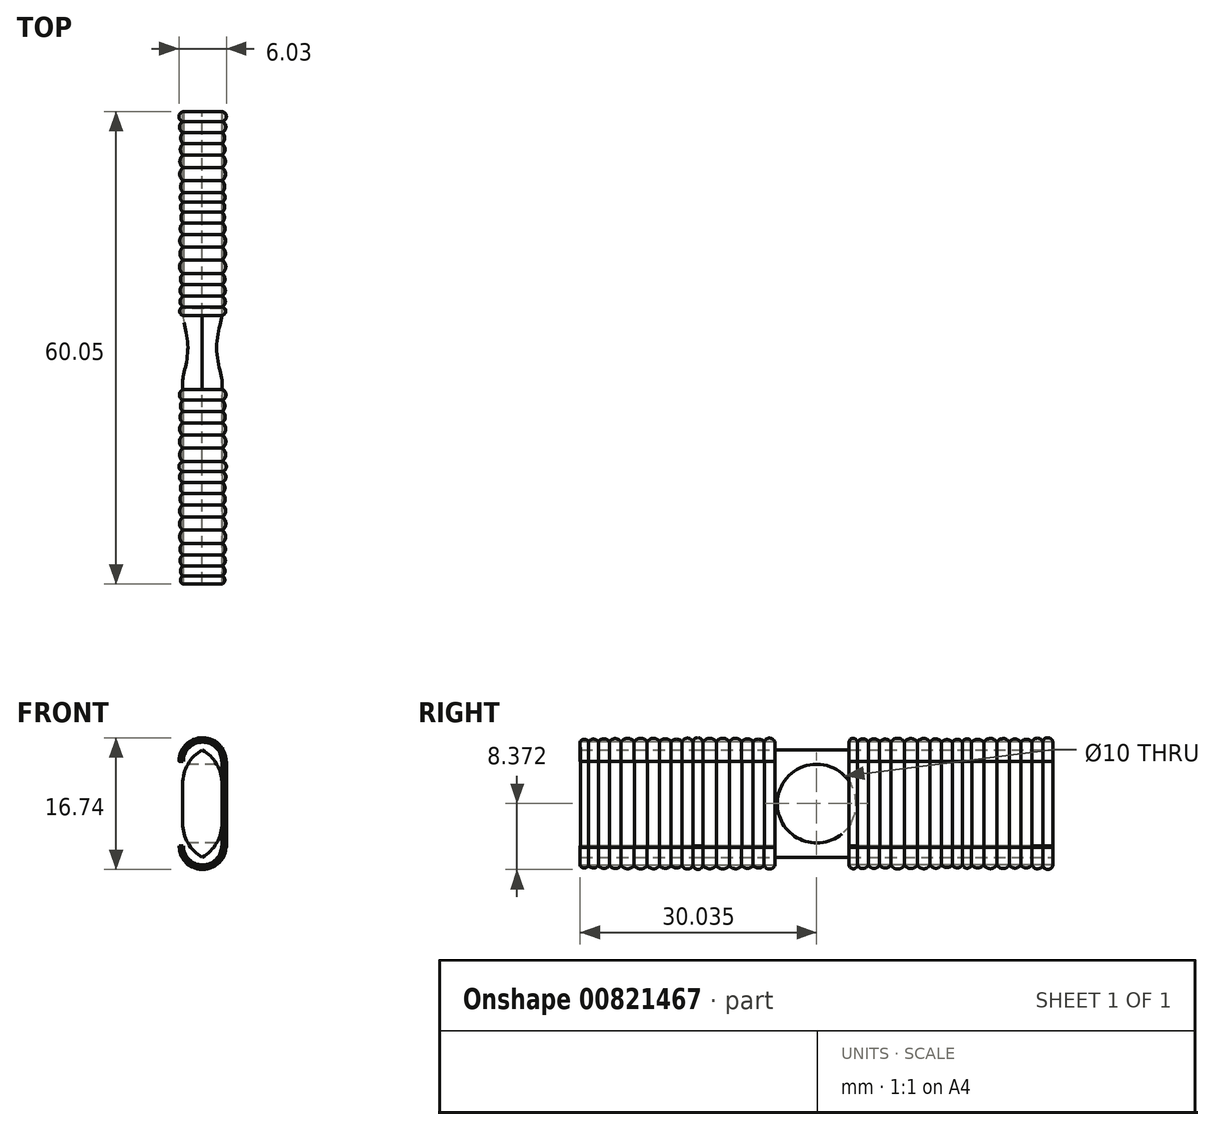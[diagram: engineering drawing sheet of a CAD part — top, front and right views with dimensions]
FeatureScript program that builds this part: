
annotation { "Feature Type Name" : "Feature", "Feature Type Description" : "" }
export const myFeature = defineFeature(function(context is Context, id is Id, definition is map)
    precondition{}
    {
        {
            var Q0;
            Q0=qCreatedBy(makeId("Right.planeOp"),FACE);
            var sketch = newSketch(context, id + "F0", { "sketchPlane" : qUnion([Q0])});
            skLineSegment(sketch, "E0.bottom", {"start": v(-22.09, 0.4) * mm, "end": v(37.91, 0.4) * mm});
            skLineSegment(sketch, "E0.top", {"start": v(-22.09, -14.6) * mm, "end": v(37.91, -14.6) * mm});
            skLineSegment(sketch, "E0.left", {"start": v(-22.09, 0.4) * mm, "end": v(-22.09, -14.6) * mm});
            skLineSegment(sketch, "E0.right", {"start": v(37.91, 0.4) * mm, "end": v(37.91, -14.6) * mm});
            skCircle(sketch, "E1", {"center": v(7.91, -7.1) * mm, "radius": 5 * mm});
            skPoint(sketch, "E1.centerSnap0", {"position": v(37.91, -7.1) * mm});
            skPoint(sketch, "E1.centerSnap1", {"position": v(7.91, 0.4) * mm});
            skLineSegment(sketch, "E2", {"start": v(37.91, -7.1) * mm, "end": v(7.91, -7.1) * mm});
            skSolve(sketch);
        }
        {
            var Q0;
            Q0=makeQuery(id+"F0.imprint","IMPRINT",FACE,{"disambiguationData":[TD([[makeQuery(id+"F0.imprint","IMPRINT",EDGE,{"derivedFrom":sQuery(id+"F0.wireOp",EDGE,"E0.bottom")}),-1.0]])]});
            extrude(context, id + "F1", {"entities" : qUnion([Q0]), "depth" : 5 * mm, "offsetDistance" : 25.4 * mm});
        }
        {
            var Q0;
            Q0=makeQuery(id+"F1.opExtrude","CAP_EDGE",EDGE,{"disambiguationData":[OSD([sQuery(id+"F0.wireOp",EDGE,"E0.top")])],"isStart":true});
            var Q1;
            Q1=makeQuery(id+"F1.opExtrude","CAP_EDGE",EDGE,{"disambiguationData":[OSD([sQuery(id+"F0.wireOp",EDGE,"E0.top")])],"isStart":false});
            var Q2;
            Q2=makeQuery(id+"F1.opExtrude","CAP_EDGE",EDGE,{"disambiguationData":[OSD([sQuery(id+"F0.wireOp",EDGE,"E0.bottom")])],"isStart":false});
            var Q3;
            Q3=makeQuery(id+"F1.opExtrude","CAP_EDGE",EDGE,{"disambiguationData":[OSD([sQuery(id+"F0.wireOp",EDGE,"E0.bottom")])],"isStart":true});
            fillet(context, id + "F2", {"entities" : qUnion([Q0, Q1, Q2, Q3]), "radius" : 5 * mm, "tangentPropagation" : true, "allowEdgeOverflow" : false});
        }
        {
            var Q0;
            Q0=qCreatedBy(makeId("Top.planeOp"),FACE);
            var sketch = newSketch(context, id + "F3", { "sketchPlane" : qUnion([Q0])});
            skLineSegment(sketch, "E3", {"start": v(5, 37.93) * mm, "end": v(5, 12.02) * mm});
            skLineSegment(sketch, "E4", {"start": v(5.04, 3.85) * mm, "end": v(5.04, -22.1) * mm});
            skArc(sketch, "E5", {"start": v(5, 36.67) * mm, "mid": v(5.57, 37.3) * mm, "end": v(5, 37.93) * mm});
            skArc(sketch, "E6", {"start": v(5, 35.28) * mm, "mid": v(5.5, 35.97) * mm, "end": v(5, 36.67) * mm});
            skArc(sketch, "E7", {"start": v(5, 33.85) * mm, "mid": v(5.36, 34.56) * mm, "end": v(5, 35.28) * mm});
            skArc(sketch, "E8", {"start": v(5, 32.4) * mm, "mid": v(5.4, 33.12) * mm, "end": v(5, 33.85) * mm});
            skArc(sketch, "E9", {"start": v(5, 30.82) * mm, "mid": v(5.45, 31.6) * mm, "end": v(5, 32.4) * mm});
            skArc(sketch, "E10", {"start": v(5, 29.16) * mm, "mid": v(5.47, 29.99) * mm, "end": v(5, 30.82) * mm});
            skArc(sketch, "E11", {"start": v(5, 27.62) * mm, "mid": v(5.36, 28.4) * mm, "end": v(5, 29.16) * mm});
            skArc(sketch, "E12", {"start": v(5, 26.42) * mm, "mid": v(5.42, 27.02) * mm, "end": v(5, 27.62) * mm});
            skArc(sketch, "E13", {"start": v(5, 25.16) * mm, "mid": v(5.37, 25.8) * mm, "end": v(5, 26.42) * mm});
            skArc(sketch, "E14", {"start": v(5, 23.78) * mm, "mid": v(5.32, 24.47) * mm, "end": v(5, 25.16) * mm});
            skArc(sketch, "E15", {"start": v(5, 22.32) * mm, "mid": v(5.41, 23.05) * mm, "end": v(5, 23.78) * mm});
            skArc(sketch, "E16", {"start": v(5, 20.72) * mm, "mid": v(5.47, 21.52) * mm, "end": v(5, 22.32) * mm});
            skArc(sketch, "E17", {"start": v(5, 19.09) * mm, "mid": v(5.45, 19.9) * mm, "end": v(5, 20.72) * mm});
            skArc(sketch, "E18", {"start": v(5, 17.35) * mm, "mid": v(5.5, 18.22) * mm, "end": v(5, 19.09) * mm});
            skArc(sketch, "E19", {"start": v(5, 15.93) * mm, "mid": v(5.39, 16.64) * mm, "end": v(5, 17.35) * mm});
            skArc(sketch, "E20", {"start": v(5, 14.48) * mm, "mid": v(5.43, 15.2) * mm, "end": v(5, 15.93) * mm});
            skArc(sketch, "E21", {"start": v(5, 13.12) * mm, "mid": v(5.44, 13.8) * mm, "end": v(5, 14.48) * mm});
            skArc(sketch, "E22", {"start": v(5, 12.02) * mm, "mid": v(5.48, 12.57) * mm, "end": v(5, 13.12) * mm});
            skLineSegment(sketch, "E23", {"start": v(5, 12.02) * mm, "end": v(5.04, 3.85) * mm});
            skLineSegment(sketch, "E24", {"start": v(5.02, 7.94) * mm, "end": v(0, 7.91) * mm});
            skArc(sketch, "E25", {"start": v(5.04, 2.63) * mm, "mid": v(5.57, 3.25) * mm, "end": v(5.04, 3.88) * mm});
            skArc(sketch, "E26", {"start": v(5.04, 1.26) * mm, "mid": v(5.51, 1.94) * mm, "end": v(5.04, 2.63) * mm});
            skArc(sketch, "E27", {"start": v(5.04, -0.16) * mm, "mid": v(5.38, 0.55) * mm, "end": v(5.04, 1.26) * mm});
            skArc(sketch, "E28", {"start": v(5.04, -1.6) * mm, "mid": v(5.43, -0.88) * mm, "end": v(5.04, -0.16) * mm});
            skArc(sketch, "E29", {"start": v(5.04, -3.17) * mm, "mid": v(5.49, -2.39) * mm, "end": v(5.04, -1.6) * mm});
            skArc(sketch, "E30", {"start": v(5.04, -4.82) * mm, "mid": v(5.5, -4) * mm, "end": v(5.04, -3.17) * mm});
            skArc(sketch, "E31", {"start": v(5.04, -6.5) * mm, "mid": v(5.48, -5.66) * mm, "end": v(5.04, -4.82) * mm});
            skArc(sketch, "E32", {"start": v(5.04, -7.8) * mm, "mid": v(5.57, -7.17) * mm, "end": v(5.04, -6.55) * mm});
            skArc(sketch, "E33", {"start": v(5.04, -9.16) * mm, "mid": v(5.51, -8.48) * mm, "end": v(5.04, -7.8) * mm});
            skArc(sketch, "E34", {"start": v(5.04, -10.58) * mm, "mid": v(5.38, -9.87) * mm, "end": v(5.04, -9.16) * mm});
            skArc(sketch, "E35", {"start": v(5.04, -12.03) * mm, "mid": v(5.43, -11.3) * mm, "end": v(5.04, -10.58) * mm});
            skArc(sketch, "E36", {"start": v(5.04, -13.6) * mm, "mid": v(5.49, -12.81) * mm, "end": v(5.04, -12.03) * mm});
            skArc(sketch, "E37", {"start": v(5.04, -15.25) * mm, "mid": v(5.5, -14.42) * mm, "end": v(5.04, -13.6) * mm});
            skArc(sketch, "E38", {"start": v(5.04, -16.92) * mm, "mid": v(5.48, -16.08) * mm, "end": v(5.04, -15.25) * mm});
            skArc(sketch, "E39", {"start": v(5.04, -18.4) * mm, "mid": v(5.45, -17.66) * mm, "end": v(5.04, -16.92) * mm});
            skArc(sketch, "E40", {"start": v(5.04, -19.8) * mm, "mid": v(5.43, -19.1) * mm, "end": v(5.04, -18.4) * mm});
            skArc(sketch, "E41", {"start": v(5.04, -21.06) * mm, "mid": v(5.39, -20.43) * mm, "end": v(5.04, -19.8) * mm});
            skArc(sketch, "E42", {"start": v(5.04, -22.1) * mm, "mid": v(5.37, -21.58) * mm, "end": v(5.04, -21.06) * mm});
            skArc(sketch, "E43.MirrorCS", {"start": v(0, 14.48) * mm, "mid": v(-0.43, 15.2) * mm, "end": v(0, 15.93) * mm});
            skArc(sketch, "E44.MirrorCS", {"start": v(-0.04, -0.16) * mm, "mid": v(-0.38, 0.55) * mm, "end": v(-0.04, 1.26) * mm});
            skArc(sketch, "E45.MirrorCS", {"start": v(0, 23.78) * mm, "mid": v(-0.32, 24.47) * mm, "end": v(0, 25.16) * mm});
            skArc(sketch, "E46.MirrorCS", {"start": v(0, 26.42) * mm, "mid": v(-0.42, 27.02) * mm, "end": v(0, 27.62) * mm});
            skArc(sketch, "E47.MirrorCS", {"start": v(0, 33.85) * mm, "mid": v(-0.36, 34.56) * mm, "end": v(0, 35.28) * mm});
            skArc(sketch, "E48.MirrorCS", {"start": v(0, 25.16) * mm, "mid": v(-0.37, 25.8) * mm, "end": v(0, 26.42) * mm});
            skArc(sketch, "E49.MirrorCS", {"start": v(-0.04, -12.03) * mm, "mid": v(-0.43, -11.3) * mm, "end": v(-0.04, -10.58) * mm});
            skLineSegment(sketch, "E50.MirrorCS", {"start": v(0, 37.93) * mm, "end": v(0, 12.02) * mm});
            skArc(sketch, "E51.MirrorCS", {"start": v(-0.04, -6.5) * mm, "mid": v(-0.48, -5.66) * mm, "end": v(-0.04, -4.82) * mm});
            skArc(sketch, "E52.MirrorCS", {"start": v(0, 22.32) * mm, "mid": v(-0.41, 23.05) * mm, "end": v(0, 23.78) * mm});
            skArc(sketch, "E53.MirrorCS", {"start": v(-0.04, -16.92) * mm, "mid": v(-0.48, -16.08) * mm, "end": v(-0.04, -15.25) * mm});
            skArc(sketch, "E54.MirrorCS", {"start": v(-0.04, -3.17) * mm, "mid": v(-0.49, -2.39) * mm, "end": v(-0.04, -1.6) * mm});
            skArc(sketch, "E55.MirrorCS", {"start": v(0, 35.28) * mm, "mid": v(-0.5, 35.97) * mm, "end": v(0, 36.67) * mm});
            skArc(sketch, "E56.MirrorCS", {"start": v(0, 13.12) * mm, "mid": v(-0.44, 13.8) * mm, "end": v(0, 14.48) * mm});
            skArc(sketch, "E57.MirrorCS", {"start": v(0, 27.62) * mm, "mid": v(-0.36, 28.4) * mm, "end": v(0, 29.16) * mm});
            skArc(sketch, "E58.MirrorCS", {"start": v(0, 32.4) * mm, "mid": v(-0.4, 33.12) * mm, "end": v(0, 33.85) * mm});
            skArc(sketch, "E59.MirrorCS", {"start": v(0, 12.02) * mm, "mid": v(-0.48, 12.57) * mm, "end": v(0, 13.12) * mm});
            skArc(sketch, "E60.MirrorCS", {"start": v(0, 15.93) * mm, "mid": v(-0.39, 16.64) * mm, "end": v(0, 17.35) * mm});
            skArc(sketch, "E61.MirrorCS", {"start": v(0, 17.35) * mm, "mid": v(-0.5, 18.22) * mm, "end": v(0, 19.09) * mm});
            skArc(sketch, "E62.MirrorCS", {"start": v(-0.04, 2.63) * mm, "mid": v(-0.57, 3.25) * mm, "end": v(-0.04, 3.88) * mm});
            skArc(sketch, "E63.MirrorCS", {"start": v(-0.04, 1.26) * mm, "mid": v(-0.51, 1.94) * mm, "end": v(-0.04, 2.63) * mm});
            skArc(sketch, "E64.MirrorCS", {"start": v(0, 36.67) * mm, "mid": v(-0.57, 37.3) * mm, "end": v(0, 37.93) * mm});
            skArc(sketch, "E65.MirrorCS", {"start": v(0, 19.09) * mm, "mid": v(-0.45, 19.9) * mm, "end": v(0, 20.72) * mm});
            skArc(sketch, "E66.MirrorCS", {"start": v(-0.04, -10.58) * mm, "mid": v(-0.38, -9.87) * mm, "end": v(-0.04, -9.16) * mm});
            skArc(sketch, "E67.MirrorCS", {"start": v(-0.04, -4.82) * mm, "mid": v(-0.5, -4) * mm, "end": v(-0.04, -3.17) * mm});
            skArc(sketch, "E68.MirrorCS", {"start": v(-0.04, -1.6) * mm, "mid": v(-0.43, -0.88) * mm, "end": v(-0.04, -0.16) * mm});
            skArc(sketch, "E69.MirrorCS", {"start": v(0, 30.82) * mm, "mid": v(-0.45, 31.6) * mm, "end": v(0, 32.4) * mm});
            skArc(sketch, "E70.MirrorCS", {"start": v(-0.04, -15.25) * mm, "mid": v(-0.5, -14.42) * mm, "end": v(-0.04, -13.6) * mm});
            skArc(sketch, "E71.MirrorCS", {"start": v(0, 20.72) * mm, "mid": v(-0.47, 21.52) * mm, "end": v(0, 22.32) * mm});
            skArc(sketch, "E72.MirrorCS", {"start": v(-0.04, -19.8) * mm, "mid": v(-0.43, -19.1) * mm, "end": v(-0.04, -18.4) * mm});
            skArc(sketch, "E73.MirrorCS", {"start": v(-0.04, -9.16) * mm, "mid": v(-0.51, -8.48) * mm, "end": v(-0.04, -7.8) * mm});
            skArc(sketch, "E74.MirrorCS", {"start": v(0, 29.16) * mm, "mid": v(-0.47, 29.99) * mm, "end": v(0, 30.82) * mm});
            skArc(sketch, "E75.MirrorCS", {"start": v(-0.04, -13.6) * mm, "mid": v(-0.49, -12.81) * mm, "end": v(-0.04, -12.03) * mm});
            skArc(sketch, "E76.MirrorCS", {"start": v(-0.04, -7.8) * mm, "mid": v(-0.57, -7.17) * mm, "end": v(-0.04, -6.55) * mm});
            skArc(sketch, "E77.MirrorCS", {"start": v(-0.04, -18.4) * mm, "mid": v(-0.45, -17.66) * mm, "end": v(-0.04, -16.92) * mm});
            skLineSegment(sketch, "E78.MirrorCS", {"start": v(0, 12.02) * mm, "end": v(-0.04, 3.85) * mm});
            skArc(sketch, "E79.MirrorCS", {"start": v(-0.04, -21.06) * mm, "mid": v(-0.39, -20.43) * mm, "end": v(-0.04, -19.8) * mm});
            skArc(sketch, "E80.MirrorCS", {"start": v(-0.04, -22.1) * mm, "mid": v(-0.37, -21.58) * mm, "end": v(-0.04, -21.06) * mm});
            skLineSegment(sketch, "E81", {"start": v(-0.04, 3.88) * mm, "end": v(-0.04, -22.1) * mm});
            skSolve(sketch);
        }
        {
            var Q0;
            {var subQ0=sQuery(id+"F3.wireOp",EDGE,"E10");Q0=makeQuery(id+"F3.imprint","IMPRINT",FACE,{"disambiguationData":[TD([[makeQuery(id+"F3.imprint","IMPRINT",EDGE,{"derivedFrom":subQ0}),1.0]])]});}
            var Q1;
            {var subQ0=sQuery(id+"F3.wireOp",EDGE,"E66.MirrorCS");Q1=makeQuery(id+"F3.imprint","IMPRINT",FACE,{"disambiguationData":[TD([[makeQuery(id+"F3.imprint","IMPRINT",EDGE,{"derivedFrom":subQ0}),-1.0]])]});}
            var Q2;
            {var subQ0=sQuery(id+"F3.wireOp",EDGE,"E71.MirrorCS");Q2=makeQuery(id+"F3.imprint","IMPRINT",FACE,{"disambiguationData":[TD([[makeQuery(id+"F3.imprint","IMPRINT",EDGE,{"derivedFrom":subQ0}),-1.0]])]});}
            var Q3;
            {var subQ0=sQuery(id+"F3.wireOp",EDGE,"E31");Q3=makeQuery(id+"F3.imprint","IMPRINT",FACE,{"disambiguationData":[TD([[makeQuery(id+"F3.imprint","IMPRINT",EDGE,{"derivedFrom":subQ0}),1.0]])]});}
            var Q4;
            {var subQ0=sQuery(id+"F3.wireOp",EDGE,"E35");Q4=makeQuery(id+"F3.imprint","IMPRINT",FACE,{"disambiguationData":[TD([[makeQuery(id+"F3.imprint","IMPRINT",EDGE,{"derivedFrom":subQ0}),1.0]])]});}
            var Q5;
            {var subQ0=sQuery(id+"F3.wireOp",EDGE,"E70.MirrorCS");Q5=makeQuery(id+"F3.imprint","IMPRINT",FACE,{"disambiguationData":[TD([[makeQuery(id+"F3.imprint","IMPRINT",EDGE,{"derivedFrom":subQ0}),-1.0]])]});}
            var Q6;
            {var subQ0=sQuery(id+"F3.wireOp",EDGE,"E19");Q6=makeQuery(id+"F3.imprint","IMPRINT",FACE,{"disambiguationData":[TD([[makeQuery(id+"F3.imprint","IMPRINT",EDGE,{"derivedFrom":subQ0}),1.0]])]});}
            var Q7;
            {var subQ0=sQuery(id+"F3.wireOp",EDGE,"E15");Q7=makeQuery(id+"F3.imprint","IMPRINT",FACE,{"disambiguationData":[TD([[makeQuery(id+"F3.imprint","IMPRINT",EDGE,{"derivedFrom":subQ0}),1.0]])]});}
            var Q8;
            {var subQ0=sQuery(id+"F3.wireOp",EDGE,"E14");Q8=makeQuery(id+"F3.imprint","IMPRINT",FACE,{"disambiguationData":[TD([[makeQuery(id+"F3.imprint","IMPRINT",EDGE,{"derivedFrom":subQ0}),1.0]])]});}
            var Q9;
            {var subQ0=sQuery(id+"F3.wireOp",EDGE,"E18");Q9=makeQuery(id+"F3.imprint","IMPRINT",FACE,{"disambiguationData":[TD([[makeQuery(id+"F3.imprint","IMPRINT",EDGE,{"derivedFrom":subQ0}),1.0]])]});}
            var Q10;
            {var subQ0=sQuery(id+"F3.wireOp",EDGE,"E53.MirrorCS");Q10=makeQuery(id+"F3.imprint","IMPRINT",FACE,{"disambiguationData":[TD([[makeQuery(id+"F3.imprint","IMPRINT",EDGE,{"derivedFrom":subQ0}),-1.0]])]});}
            var Q11;
            {var subQ0=sQuery(id+"F3.wireOp",EDGE,"E54.MirrorCS");Q11=makeQuery(id+"F3.imprint","IMPRINT",FACE,{"disambiguationData":[TD([[makeQuery(id+"F3.imprint","IMPRINT",EDGE,{"derivedFrom":subQ0}),-1.0]])]});}
            var Q12;
            {var subQ0=sQuery(id+"F3.wireOp",EDGE,"E65.MirrorCS");Q12=makeQuery(id+"F3.imprint","IMPRINT",FACE,{"disambiguationData":[TD([[makeQuery(id+"F3.imprint","IMPRINT",EDGE,{"derivedFrom":subQ0}),-1.0]])]});}
            var Q13;
            {var subQ0=sQuery(id+"F3.wireOp",EDGE,"E67.MirrorCS");Q13=makeQuery(id+"F3.imprint","IMPRINT",FACE,{"disambiguationData":[TD([[makeQuery(id+"F3.imprint","IMPRINT",EDGE,{"derivedFrom":subQ0}),-1.0]])]});}
            var Q14;
            {var subQ0=sQuery(id+"F3.wireOp",EDGE,"E21");Q14=makeQuery(id+"F3.imprint","IMPRINT",FACE,{"disambiguationData":[TD([[makeQuery(id+"F3.imprint","IMPRINT",EDGE,{"derivedFrom":subQ0}),1.0]])]});}
            var Q15;
            {var subQ0=sQuery(id+"F3.wireOp",EDGE,"E51.MirrorCS");Q15=makeQuery(id+"F3.imprint","IMPRINT",FACE,{"disambiguationData":[TD([[makeQuery(id+"F3.imprint","IMPRINT",EDGE,{"derivedFrom":subQ0}),-1.0]])]});}
            var Q16;
            {var subQ0=sQuery(id+"F3.wireOp",EDGE,"E11");Q16=makeQuery(id+"F3.imprint","IMPRINT",FACE,{"disambiguationData":[TD([[makeQuery(id+"F3.imprint","IMPRINT",EDGE,{"derivedFrom":subQ0}),1.0]])]});}
            var Q17;
            {var subQ0=sQuery(id+"F3.wireOp",EDGE,"E75.MirrorCS");Q17=makeQuery(id+"F3.imprint","IMPRINT",FACE,{"disambiguationData":[TD([[makeQuery(id+"F3.imprint","IMPRINT",EDGE,{"derivedFrom":subQ0}),-1.0]])]});}
            var Q18;
            {var subQ0=sQuery(id+"F3.wireOp",EDGE,"E16");Q18=makeQuery(id+"F3.imprint","IMPRINT",FACE,{"disambiguationData":[TD([[makeQuery(id+"F3.imprint","IMPRINT",EDGE,{"derivedFrom":subQ0}),1.0]])]});}
            var Q19;
            {var subQ0=sQuery(id+"F3.wireOp",EDGE,"E43.MirrorCS");Q19=makeQuery(id+"F3.imprint","IMPRINT",FACE,{"disambiguationData":[TD([[makeQuery(id+"F3.imprint","IMPRINT",EDGE,{"derivedFrom":subQ0}),-1.0]])]});}
            var Q20;
            {var subQ0=sQuery(id+"F3.wireOp",EDGE,"E36");Q20=makeQuery(id+"F3.imprint","IMPRINT",FACE,{"disambiguationData":[TD([[makeQuery(id+"F3.imprint","IMPRINT",EDGE,{"derivedFrom":subQ0}),1.0]])]});}
            var Q21;
            {var subQ0=sQuery(id+"F3.wireOp",EDGE,"E27");Q21=makeQuery(id+"F3.imprint","IMPRINT",FACE,{"disambiguationData":[TD([[makeQuery(id+"F3.imprint","IMPRINT",EDGE,{"derivedFrom":subQ0}),1.0]])]});}
            var Q22;
            {var subQ0=sQuery(id+"F3.wireOp",EDGE,"E29");Q22=makeQuery(id+"F3.imprint","IMPRINT",FACE,{"disambiguationData":[TD([[makeQuery(id+"F3.imprint","IMPRINT",EDGE,{"derivedFrom":subQ0}),1.0]])]});}
            var Q23;
            {var subQ0=sQuery(id+"F3.wireOp",EDGE,"E61.MirrorCS");Q23=makeQuery(id+"F3.imprint","IMPRINT",FACE,{"disambiguationData":[TD([[makeQuery(id+"F3.imprint","IMPRINT",EDGE,{"derivedFrom":subQ0}),-1.0]])]});}
            var Q24;
            {var subQ0=sQuery(id+"F3.wireOp",EDGE,"E52.MirrorCS");Q24=makeQuery(id+"F3.imprint","IMPRINT",FACE,{"disambiguationData":[TD([[makeQuery(id+"F3.imprint","IMPRINT",EDGE,{"derivedFrom":subQ0}),-1.0]])]});}
            var Q25;
            {var subQ0=sQuery(id+"F3.wireOp",EDGE,"E17");Q25=makeQuery(id+"F3.imprint","IMPRINT",FACE,{"disambiguationData":[TD([[makeQuery(id+"F3.imprint","IMPRINT",EDGE,{"derivedFrom":subQ0}),1.0]])]});}
            var Q26;
            {var subQ0=sQuery(id+"F3.wireOp",EDGE,"E30");Q26=makeQuery(id+"F3.imprint","IMPRINT",FACE,{"disambiguationData":[TD([[makeQuery(id+"F3.imprint","IMPRINT",EDGE,{"derivedFrom":subQ0}),1.0]])]});}
            var Q27;
            {var subQ0=sQuery(id+"F3.wireOp",EDGE,"E33");Q27=makeQuery(id+"F3.imprint","IMPRINT",FACE,{"disambiguationData":[TD([[makeQuery(id+"F3.imprint","IMPRINT",EDGE,{"derivedFrom":subQ0}),1.0]])]});}
            var Q28;
            {var subQ0=sQuery(id+"F3.wireOp",EDGE,"E68.MirrorCS");Q28=makeQuery(id+"F3.imprint","IMPRINT",FACE,{"disambiguationData":[TD([[makeQuery(id+"F3.imprint","IMPRINT",EDGE,{"derivedFrom":subQ0}),-1.0]])]});}
            var Q29;
            {var subQ0=sQuery(id+"F3.wireOp",EDGE,"E63.MirrorCS");Q29=makeQuery(id+"F3.imprint","IMPRINT",FACE,{"disambiguationData":[TD([[makeQuery(id+"F3.imprint","IMPRINT",EDGE,{"derivedFrom":subQ0}),-1.0]])]});}
            var Q30;
            {var subQ0=sQuery(id+"F3.wireOp",EDGE,"E9");Q30=makeQuery(id+"F3.imprint","IMPRINT",FACE,{"disambiguationData":[TD([[makeQuery(id+"F3.imprint","IMPRINT",EDGE,{"derivedFrom":subQ0}),1.0]])]});}
            var Q31;
            {var subQ0=sQuery(id+"F3.wireOp",EDGE,"E26");Q31=makeQuery(id+"F3.imprint","IMPRINT",FACE,{"disambiguationData":[TD([[makeQuery(id+"F3.imprint","IMPRINT",EDGE,{"derivedFrom":subQ0}),1.0]])]});}
            var Q32;
            {var subQ0=sQuery(id+"F3.wireOp",EDGE,"E76.MirrorCS");Q32=makeQuery(id+"F3.imprint","IMPRINT",FACE,{"disambiguationData":[TD([[makeQuery(id+"F3.imprint","IMPRINT",EDGE,{"derivedFrom":subQ0}),-1.0]])]});}
            var Q33;
            {var subQ0=sQuery(id+"F3.wireOp",EDGE,"E22");Q33=makeQuery(id+"F3.imprint","IMPRINT",FACE,{"disambiguationData":[TD([[makeQuery(id+"F3.imprint","IMPRINT",EDGE,{"derivedFrom":subQ0}),1.0]])]});}
            var Q34;
            {var subQ0=sQuery(id+"F3.wireOp",EDGE,"E60.MirrorCS");Q34=makeQuery(id+"F3.imprint","IMPRINT",FACE,{"disambiguationData":[TD([[makeQuery(id+"F3.imprint","IMPRINT",EDGE,{"derivedFrom":subQ0}),-1.0]])]});}
            var Q35;
            {var subQ0=sQuery(id+"F3.wireOp",EDGE,"E73.MirrorCS");Q35=makeQuery(id+"F3.imprint","IMPRINT",FACE,{"disambiguationData":[TD([[makeQuery(id+"F3.imprint","IMPRINT",EDGE,{"derivedFrom":subQ0}),-1.0]])]});}
            var Q36;
            {var subQ0=sQuery(id+"F3.wireOp",EDGE,"E13");Q36=makeQuery(id+"F3.imprint","IMPRINT",FACE,{"disambiguationData":[TD([[makeQuery(id+"F3.imprint","IMPRINT",EDGE,{"derivedFrom":subQ0}),1.0]])]});}
            var Q37;
            {var subQ3=sQuery(id+"F3.wireOp",EDGE,"E25");Q37=makeQuery(id+"F3.imprint","IMPRINT",FACE,{"disambiguationData":[TD([[makeQuery(id+"F3.imprint","IMPRINT",EDGE,{"derivedFrom":subQ3}),1.0]])]});}
            var Q38;
            {var subQ0=sQuery(id+"F3.wireOp",EDGE,"E46.MirrorCS");Q38=makeQuery(id+"F3.imprint","IMPRINT",FACE,{"disambiguationData":[TD([[makeQuery(id+"F3.imprint","IMPRINT",EDGE,{"derivedFrom":subQ0}),-1.0]])]});}
            var Q39;
            {var subQ0=sQuery(id+"F3.wireOp",EDGE,"E20");Q39=makeQuery(id+"F3.imprint","IMPRINT",FACE,{"disambiguationData":[TD([[makeQuery(id+"F3.imprint","IMPRINT",EDGE,{"derivedFrom":subQ0}),1.0]])]});}
            var Q40;
            {var subQ0=sQuery(id+"F3.wireOp",EDGE,"E49.MirrorCS");Q40=makeQuery(id+"F3.imprint","IMPRINT",FACE,{"disambiguationData":[TD([[makeQuery(id+"F3.imprint","IMPRINT",EDGE,{"derivedFrom":subQ0}),-1.0]])]});}
            var Q41;
            {var subQ0=sQuery(id+"F3.wireOp",EDGE,"E34");Q41=makeQuery(id+"F3.imprint","IMPRINT",FACE,{"disambiguationData":[TD([[makeQuery(id+"F3.imprint","IMPRINT",EDGE,{"derivedFrom":subQ0}),1.0]])]});}
            var Q42;
            {var subQ0=sQuery(id+"F3.wireOp",EDGE,"E32");Q42=makeQuery(id+"F3.imprint","IMPRINT",FACE,{"disambiguationData":[TD([[makeQuery(id+"F3.imprint","IMPRINT",EDGE,{"derivedFrom":subQ0}),1.0]])]});}
            var Q43;
            {var subQ0=sQuery(id+"F3.wireOp",EDGE,"E48.MirrorCS");Q43=makeQuery(id+"F3.imprint","IMPRINT",FACE,{"disambiguationData":[TD([[makeQuery(id+"F3.imprint","IMPRINT",EDGE,{"derivedFrom":subQ0}),-1.0]])]});}
            var Q44;
            {var subQ0=sQuery(id+"F3.wireOp",EDGE,"E28");Q44=makeQuery(id+"F3.imprint","IMPRINT",FACE,{"disambiguationData":[TD([[makeQuery(id+"F3.imprint","IMPRINT",EDGE,{"derivedFrom":subQ0}),1.0]])]});}
            var Q45;
            {var subQ0=sQuery(id+"F3.wireOp",EDGE,"E59.MirrorCS");Q45=makeQuery(id+"F3.imprint","IMPRINT",FACE,{"disambiguationData":[TD([[makeQuery(id+"F3.imprint","IMPRINT",EDGE,{"derivedFrom":subQ0}),-1.0]])]});}
            var Q46;
            {var subQ0=sQuery(id+"F3.wireOp",EDGE,"E44.MirrorCS");Q46=makeQuery(id+"F3.imprint","IMPRINT",FACE,{"disambiguationData":[TD([[makeQuery(id+"F3.imprint","IMPRINT",EDGE,{"derivedFrom":subQ0}),-1.0]])]});}
            var Q47;
            {var subQ0=sQuery(id+"F3.wireOp",EDGE,"E62.MirrorCS");Q47=makeQuery(id+"F3.imprint","IMPRINT",FACE,{"disambiguationData":[TD([[makeQuery(id+"F3.imprint","IMPRINT",EDGE,{"derivedFrom":subQ0}),-1.0]])]});}
            var Q48;
            {var subQ0=sQuery(id+"F3.wireOp",EDGE,"E56.MirrorCS");Q48=makeQuery(id+"F3.imprint","IMPRINT",FACE,{"disambiguationData":[TD([[makeQuery(id+"F3.imprint","IMPRINT",EDGE,{"derivedFrom":subQ0}),-1.0]])]});}
            var Q49;
            {var subQ0=sQuery(id+"F3.wireOp",EDGE,"E57.MirrorCS");Q49=makeQuery(id+"F3.imprint","IMPRINT",FACE,{"disambiguationData":[TD([[makeQuery(id+"F3.imprint","IMPRINT",EDGE,{"derivedFrom":subQ0}),-1.0]])]});}
            var Q50;
            {var subQ0=sQuery(id+"F3.wireOp",EDGE,"E39");Q50=makeQuery(id+"F3.imprint","IMPRINT",FACE,{"disambiguationData":[TD([[makeQuery(id+"F3.imprint","IMPRINT",EDGE,{"derivedFrom":subQ0}),1.0]])]});}
            var Q51;
            {var subQ0=sQuery(id+"F3.wireOp",EDGE,"E37");Q51=makeQuery(id+"F3.imprint","IMPRINT",FACE,{"disambiguationData":[TD([[makeQuery(id+"F3.imprint","IMPRINT",EDGE,{"derivedFrom":subQ0}),1.0]])]});}
            var Q52;
            {var subQ0=sQuery(id+"F3.wireOp",EDGE,"E38");Q52=makeQuery(id+"F3.imprint","IMPRINT",FACE,{"disambiguationData":[TD([[makeQuery(id+"F3.imprint","IMPRINT",EDGE,{"derivedFrom":subQ0}),1.0]])]});}
            var Q53;
            {var subQ0=sQuery(id+"F3.wireOp",EDGE,"E40");Q53=makeQuery(id+"F3.imprint","IMPRINT",FACE,{"disambiguationData":[TD([[makeQuery(id+"F3.imprint","IMPRINT",EDGE,{"derivedFrom":subQ0}),1.0]])]});}
            var Q54;
            {var subQ0=sQuery(id+"F3.wireOp",EDGE,"E72.MirrorCS");Q54=makeQuery(id+"F3.imprint","IMPRINT",FACE,{"disambiguationData":[TD([[makeQuery(id+"F3.imprint","IMPRINT",EDGE,{"derivedFrom":subQ0}),-1.0]])]});}
            var Q55;
            {var subQ0=sQuery(id+"F3.wireOp",EDGE,"E77.MirrorCS");Q55=makeQuery(id+"F3.imprint","IMPRINT",FACE,{"disambiguationData":[TD([[makeQuery(id+"F3.imprint","IMPRINT",EDGE,{"derivedFrom":subQ0}),-1.0]])]});}
            var Q56;
            {var subQ0=sQuery(id+"F3.wireOp",EDGE,"E41");Q56=makeQuery(id+"F3.imprint","IMPRINT",FACE,{"disambiguationData":[TD([[makeQuery(id+"F3.imprint","IMPRINT",EDGE,{"derivedFrom":subQ0}),1.0]])]});}
            var Q57;
            {var subQ0=sQuery(id+"F3.wireOp",EDGE,"E79.MirrorCS");Q57=makeQuery(id+"F3.imprint","IMPRINT",FACE,{"disambiguationData":[TD([[makeQuery(id+"F3.imprint","IMPRINT",EDGE,{"derivedFrom":subQ0}),-1.0]])]});}
            var Q58;
            {var subQ0=sQuery(id+"F3.wireOp",EDGE,"E42");Q58=makeQuery(id+"F3.imprint","IMPRINT",FACE,{"disambiguationData":[TD([[makeQuery(id+"F3.imprint","IMPRINT",EDGE,{"derivedFrom":subQ0}),1.0]])]});}
            var Q59;
            {var subQ0=sQuery(id+"F3.wireOp",EDGE,"E80.MirrorCS");Q59=makeQuery(id+"F3.imprint","IMPRINT",FACE,{"disambiguationData":[TD([[makeQuery(id+"F3.imprint","IMPRINT",EDGE,{"derivedFrom":subQ0}),-1.0]])]});}
            var Q60;
            {var subQ0=sQuery(id+"F3.wireOp",EDGE,"E7");Q60=makeQuery(id+"F3.imprint","IMPRINT",FACE,{"disambiguationData":[TD([[makeQuery(id+"F3.imprint","IMPRINT",EDGE,{"derivedFrom":subQ0}),1.0]])]});}
            var Q61;
            {var subQ0=sQuery(id+"F3.wireOp",EDGE,"E8");Q61=makeQuery(id+"F3.imprint","IMPRINT",FACE,{"disambiguationData":[TD([[makeQuery(id+"F3.imprint","IMPRINT",EDGE,{"derivedFrom":subQ0}),1.0]])]});}
            var Q62;
            {var subQ0=sQuery(id+"F3.wireOp",EDGE,"E69.MirrorCS");Q62=makeQuery(id+"F3.imprint","IMPRINT",FACE,{"disambiguationData":[TD([[makeQuery(id+"F3.imprint","IMPRINT",EDGE,{"derivedFrom":subQ0}),-1.0]])]});}
            var Q63;
            {var subQ0=sQuery(id+"F3.wireOp",EDGE,"E5");Q63=makeQuery(id+"F3.imprint","IMPRINT",FACE,{"disambiguationData":[TD([[makeQuery(id+"F3.imprint","IMPRINT",EDGE,{"derivedFrom":subQ0}),1.0]])]});}
            var Q64;
            {var subQ0=sQuery(id+"F3.wireOp",EDGE,"E58.MirrorCS");Q64=makeQuery(id+"F3.imprint","IMPRINT",FACE,{"disambiguationData":[TD([[makeQuery(id+"F3.imprint","IMPRINT",EDGE,{"derivedFrom":subQ0}),-1.0]])]});}
            var Q65;
            {var subQ0=sQuery(id+"F3.wireOp",EDGE,"E74.MirrorCS");Q65=makeQuery(id+"F3.imprint","IMPRINT",FACE,{"disambiguationData":[TD([[makeQuery(id+"F3.imprint","IMPRINT",EDGE,{"derivedFrom":subQ0}),-1.0]])]});}
            var Q66;
            {var subQ0=sQuery(id+"F3.wireOp",EDGE,"E12");Q66=makeQuery(id+"F3.imprint","IMPRINT",FACE,{"disambiguationData":[TD([[makeQuery(id+"F3.imprint","IMPRINT",EDGE,{"derivedFrom":subQ0}),1.0]])]});}
            var Q67;
            {var subQ0=sQuery(id+"F3.wireOp",EDGE,"E64.MirrorCS");Q67=makeQuery(id+"F3.imprint","IMPRINT",FACE,{"disambiguationData":[TD([[makeQuery(id+"F3.imprint","IMPRINT",EDGE,{"derivedFrom":subQ0}),-1.0]])]});}
            var Q68;
            {var subQ0=sQuery(id+"F3.wireOp",EDGE,"E6");Q68=makeQuery(id+"F3.imprint","IMPRINT",FACE,{"disambiguationData":[TD([[makeQuery(id+"F3.imprint","IMPRINT",EDGE,{"derivedFrom":subQ0}),1.0]])]});}
            var Q69;
            {var subQ0=sQuery(id+"F3.wireOp",EDGE,"E45.MirrorCS");Q69=makeQuery(id+"F3.imprint","IMPRINT",FACE,{"disambiguationData":[TD([[makeQuery(id+"F3.imprint","IMPRINT",EDGE,{"derivedFrom":subQ0}),-1.0]])]});}
            var Q70;
            {var subQ0=sQuery(id+"F3.wireOp",EDGE,"E55.MirrorCS");Q70=makeQuery(id+"F3.imprint","IMPRINT",FACE,{"disambiguationData":[TD([[makeQuery(id+"F3.imprint","IMPRINT",EDGE,{"derivedFrom":subQ0}),-1.0]])]});}
            var Q71;
            {var subQ0=sQuery(id+"F3.wireOp",EDGE,"E47.MirrorCS");Q71=makeQuery(id+"F3.imprint","IMPRINT",FACE,{"disambiguationData":[TD([[makeQuery(id+"F3.imprint","IMPRINT",EDGE,{"derivedFrom":subQ0}),-1.0]])]});}
            var Q72;
            Q72=sQuery(id+"F3.wireOp",EDGE,"E24");
            var Q73;
            Q73=sQuery(id+"F3.wireOp",EDGE,"E23");
            var Q74;
            Q74=sQuery(id+"F3.wireOp",EDGE,"E78.MirrorCS");
            var Q75;
            Q75=sQuery(id+"F3.wireOp",EDGE,"E34");
            var Q76;
            Q76=sQuery(id+"F3.wireOp",EDGE,"E80.MirrorCS");
            var Q77;
            Q77=sQuery(id+"F3.wireOp",EDGE,"E69.MirrorCS");
            var Q78;
            Q78=sQuery(id+"F3.wireOp",EDGE,"E28");
            var Q79;
            Q79=sQuery(id+"F3.wireOp",EDGE,"E65.MirrorCS");
            var Q80;
            Q80=sQuery(id+"F3.wireOp",EDGE,"E79.MirrorCS");
            var Q81;
            Q81=sQuery(id+"F3.wireOp",EDGE,"E49.MirrorCS");
            var Q82;
            Q82=sQuery(id+"F3.wireOp",EDGE,"E30");
            var Q83;
            Q83=sQuery(id+"F3.wireOp",EDGE,"E75.MirrorCS");
            var Q84;
            Q84=sQuery(id+"F3.wireOp",EDGE,"E71.MirrorCS");
            var Q85;
            Q85=sQuery(id+"F3.wireOp",EDGE,"E33");
            var Q86;
            Q86=sQuery(id+"F3.wireOp",EDGE,"E58.MirrorCS");
            var Q87;
            Q87=sQuery(id+"F3.wireOp",EDGE,"E46.MirrorCS");
            var Q88;
            Q88=sQuery(id+"F3.wireOp",EDGE,"E81");
            var Q89;
            Q89=sQuery(id+"F3.wireOp",EDGE,"E60.MirrorCS");
            var Q90;
            Q90=sQuery(id+"F3.wireOp",EDGE,"E3");
            var Q91;
            Q91=sQuery(id+"F3.wireOp",EDGE,"E76.MirrorCS");
            var Q92;
            Q92=sQuery(id+"F3.wireOp",EDGE,"E74.MirrorCS");
            var Q93;
            Q93=sQuery(id+"F3.wireOp",EDGE,"E67.MirrorCS");
            var Q94;
            Q94=sQuery(id+"F3.wireOp",EDGE,"E7");
            var Q95;
            Q95=sQuery(id+"F3.wireOp",EDGE,"E51.MirrorCS");
            var Q96;
            Q96=sQuery(id+"F3.wireOp",EDGE,"E29");
            var Q97;
            Q97=sQuery(id+"F3.wireOp",EDGE,"E10");
            var Q98;
            Q98=sQuery(id+"F3.wireOp",EDGE,"E27");
            var Q99;
            Q99=sQuery(id+"F3.wireOp",EDGE,"E63.MirrorCS");
            var Q100;
            Q100=sQuery(id+"F3.wireOp",EDGE,"E32");
            var Q101;
            Q101=sQuery(id+"F3.wireOp",EDGE,"E52.MirrorCS");
            var Q102;
            Q102=sQuery(id+"F3.wireOp",EDGE,"E35");
            var Q103;
            Q103=sQuery(id+"F3.wireOp",EDGE,"E53.MirrorCS");
            var Q104;
            Q104=sQuery(id+"F3.wireOp",EDGE,"E56.MirrorCS");
            var Q105;
            Q105=sQuery(id+"F3.wireOp",EDGE,"E66.MirrorCS");
            var Q106;
            Q106=sQuery(id+"F3.wireOp",EDGE,"E9");
            var Q107;
            Q107=sQuery(id+"F3.wireOp",EDGE,"E70.MirrorCS");
            var Q108;
            Q108=sQuery(id+"F3.wireOp",EDGE,"E77.MirrorCS");
            var Q109;
            Q109=sQuery(id+"F3.wireOp",EDGE,"E72.MirrorCS");
            var Q110;
            Q110=sQuery(id+"F3.wireOp",EDGE,"E61.MirrorCS");
            var Q111;
            Q111=sQuery(id+"F3.wireOp",EDGE,"E31");
            var Q112;
            Q112=sQuery(id+"F3.wireOp",EDGE,"E36");
            var Q113;
            Q113=sQuery(id+"F3.wireOp",EDGE,"E15");
            var Q114;
            Q114=sQuery(id+"F3.wireOp",EDGE,"E45.MirrorCS");
            var Q115;
            Q115=sQuery(id+"F3.wireOp",EDGE,"E48.MirrorCS");
            var Q116;
            Q116=sQuery(id+"F3.wireOp",EDGE,"E47.MirrorCS");
            var Q117;
            Q117=sQuery(id+"F3.wireOp",EDGE,"E4");
            var Q118;
            Q118=sQuery(id+"F3.wireOp",EDGE,"E8");
            var Q119;
            Q119=sQuery(id+"F3.wireOp",EDGE,"E50.MirrorCS");
            var Q120;
            Q120=sQuery(id+"F3.wireOp",EDGE,"E43.MirrorCS");
            var Q121;
            Q121=sQuery(id+"F3.wireOp",EDGE,"E73.MirrorCS");
            var Q122;
            Q122=sQuery(id+"F3.wireOp",EDGE,"E57.MirrorCS");
            var Q123;
            Q123=sQuery(id+"F3.wireOp",EDGE,"E16");
            var Q124;
            Q124=sQuery(id+"F3.wireOp",EDGE,"E17");
            var Q125;
            Q125=sQuery(id+"F3.wireOp",EDGE,"E19");
            var Q126;
            Q126=sQuery(id+"F3.wireOp",EDGE,"E5");
            var Q127;
            Q127=sQuery(id+"F3.wireOp",EDGE,"E44.MirrorCS");
            var Q128;
            Q128=sQuery(id+"F3.wireOp",EDGE,"E14");
            var Q129;
            Q129=sQuery(id+"F3.wireOp",EDGE,"E62.MirrorCS");
            var Q130;
            Q130=sQuery(id+"F3.wireOp",EDGE,"E11");
            var Q131;
            Q131=sQuery(id+"F3.wireOp",EDGE,"E37");
            var Q132;
            Q132=sQuery(id+"F3.wireOp",EDGE,"E25");
            var Q133;
            Q133=sQuery(id+"F3.wireOp",EDGE,"E13");
            var Q134;
            Q134=sQuery(id+"F3.wireOp",EDGE,"E38");
            var Q135;
            Q135=sQuery(id+"F3.wireOp",EDGE,"E20");
            var Q136;
            Q136=sQuery(id+"F3.wireOp",EDGE,"E22");
            var Q137;
            Q137=sQuery(id+"F3.wireOp",EDGE,"E64.MirrorCS");
            var Q138;
            Q138=sQuery(id+"F3.wireOp",EDGE,"E55.MirrorCS");
            var Q139;
            Q139=sQuery(id+"F3.wireOp",EDGE,"E40");
            var Q140;
            Q140=sQuery(id+"F3.wireOp",EDGE,"E39");
            var Q141;
            Q141=sQuery(id+"F3.wireOp",EDGE,"E54.MirrorCS");
            var Q142;
            Q142=sQuery(id+"F3.wireOp",EDGE,"E68.MirrorCS");
            var Q143;
            Q143=sQuery(id+"F3.wireOp",EDGE,"E12");
            var Q144;
            Q144=sQuery(id+"F3.wireOp",EDGE,"E59.MirrorCS");
            var Q145;
            Q145=sQuery(id+"F3.wireOp",EDGE,"E6");
            var Q146;
            Q146=sQuery(id+"F3.wireOp",EDGE,"E42");
            var Q147;
            Q147=sQuery(id+"F3.wireOp",EDGE,"E21");
            var Q148;
            Q148=sQuery(id+"F3.wireOp",EDGE,"E26");
            var Q149;
            Q149=sQuery(id+"F3.wireOp",EDGE,"E41");
            var Q150;
            Q150=sQuery(id+"F3.wireOp",EDGE,"E18");
            extrude(context, id + "F4", {"entities" : qUnion([Q0, Q1, Q2, Q3, Q4, Q5, Q6, Q7, Q8, Q9, Q10, Q11, Q12, Q13, Q14, Q15, Q16, Q17, Q18, Q19, Q20, Q21, Q22, Q23, Q24, Q25, Q26, Q27, Q28, Q29, Q30, Q31, Q32, Q33, Q34, Q35, Q36, Q37, Q38, Q39, Q40, Q41, Q42, Q43, Q44, Q45, Q46, Q47, Q48, Q49, Q50, Q51, Q52, Q53, Q54, Q55, Q56, Q57, Q58, Q59, Q60, Q61, Q62, Q63, Q64, Q65, Q66, Q67, Q68, Q69, Q70, Q71]), "surfaceEntities" : qUnion([Q72, Q73, Q74, Q75, Q76, Q77, Q78, Q79, Q80, Q81, Q82, Q83, Q84, Q85, Q86, Q87, Q88, Q89, Q90, Q91, Q92, Q93, Q94, Q95, Q96, Q97, Q98, Q99, Q100, Q101, Q102, Q103, Q104, Q105, Q106, Q107, Q108, Q109, Q110, Q111, Q112, Q113, Q114, Q115, Q116, Q117, Q118, Q119, Q120, Q121, Q122, Q123, Q124, Q125, Q126, Q127, Q128, Q129, Q130, Q131, Q132, Q133, Q134, Q135, Q136, Q137, Q138, Q139, Q140, Q141, Q142, Q143, Q144, Q145, Q146, Q147, Q148, Q149, Q150]), "oppositeDirection" : true, "depth" : 12.7 * mm, "offsetDistance" : 25.4 * mm});
        }
        {
            var Q0;
            Q0=makeQuery(id+"F1.opExtrude","SWEPT_FACE",FACE,{"disambiguationData":[OSD([sQuery(id+"F0.wireOp",EDGE,"E0.left")])]});
            var sketch = newSketch(context, id + "F5", { "sketchPlane" : qUnion([Q0])});
            skLineSegment(sketch, "E82.bottom", {"start": v(4.44, 1.5) * mm, "end": v(7.34, 1.5) * mm});
            skLineSegment(sketch, "E82.top", {"start": v(4.44, -1.73) * mm, "end": v(7.34, -1.73) * mm});
            skLineSegment(sketch, "E82.left", {"start": v(4.44, 1.5) * mm, "end": v(4.44, -1.73) * mm});
            skLineSegment(sketch, "E82.right", {"start": v(7.34, 1.5) * mm, "end": v(7.34, -1.73) * mm});
            skPoint(sketch, "E83.oppositeSnap0", {"position": v(0.67, -2.1) * mm});
            skLineSegment(sketch, "E83.bottom", {"start": v(-1.72, 1.7) * mm, "end": v(0.67, 1.7) * mm});
            skLineSegment(sketch, "E83.top", {"start": v(-1.72, -1.73) * mm, "end": v(0.67, -1.73) * mm});
            skLineSegment(sketch, "E83.left", {"start": v(-1.72, 1.7) * mm, "end": v(-1.72, -1.73) * mm});
            skLineSegment(sketch, "E83.right", {"start": v(0.67, 1.7) * mm, "end": v(0.67, -1.73) * mm});
            skSolve(sketch);
        }
        {
            var Q0;
            Q0=makeQuery(id+"F5.imprint","IMPRINT",FACE,{"disambiguationData":[TD([[makeQuery(id+"F5.imprint","IMPRINT",EDGE,{"derivedFrom":sQuery(id+"F5.wireOp",EDGE,"E83.bottom")}),-1.0]])]});
            extrude(context, id + "F6", {"entities" : qUnion([Q0]), "operationType" : NewBodyOperationType.REMOVE, "oppositeDirection" : true, "depth" : 5080 * mm, "offsetDistance" : 25.4 * mm});
        }
        {
            var Q0;
            Q0=makeQuery(id+"F5.imprint","IMPRINT",FACE,{"disambiguationData":[TD([[makeQuery(id+"F5.imprint","IMPRINT",EDGE,{"derivedFrom":sQuery(id+"F5.wireOp",EDGE,"E82.bottom")}),-1.0]])]});
            extrude(context, id + "F7", {"entities" : qUnion([Q0]), "operationType" : NewBodyOperationType.REMOVE, "endBound" : BoundingType.THROUGH_ALL, "oppositeDirection" : true, "depth" : 25.4 * mm, "offsetDistance" : 25.4 * mm});
        }
        {
            var Q0;
            {var subQ0=sQuery(id+"F3.wireOp",EDGE,"E14");Q0=makeQuery(id+"F7.boolean.opBoolean","COPY",FACE,{"disambiguationData":[TD([makeQuery(id+"F4.opExtrude","SWEPT_FACE",FACE,{"disambiguationData":[OSD([subQ0])]})])],"derivedFrom":makeQuery(id+"F7.opExtrude","SWEPT_FACE",FACE,{"disambiguationData":[OSD([sQuery(id+"F5.wireOp",EDGE,"E82.top")])]})});}
            var sketch = newSketch(context, id + "F8", { "sketchPlane" : qUnion([Q0])});
            skLineSegment(sketch, "E84", {"start": v(4.96, 37.92) * mm, "end": v(4.96, 12) * mm});
            skLineSegment(sketch, "E85", {"start": v(5, 3.84) * mm, "end": v(5, -22.12) * mm});
            skArc(sketch, "E86", {"start": v(4.96, 36.65) * mm, "mid": v(5.53, 37.28) * mm, "end": v(4.96, 37.92) * mm});
            skArc(sketch, "E87", {"start": v(4.96, 35.27) * mm, "mid": v(5.47, 35.96) * mm, "end": v(4.96, 36.65) * mm});
            skArc(sketch, "E88", {"start": v(4.96, 33.83) * mm, "mid": v(5.32, 34.55) * mm, "end": v(4.96, 35.27) * mm});
            skArc(sketch, "E89", {"start": v(4.96, 32.38) * mm, "mid": v(5.36, 33.1) * mm, "end": v(4.96, 33.83) * mm});
            skArc(sketch, "E90", {"start": v(4.96, 30.8) * mm, "mid": v(5.42, 31.6) * mm, "end": v(4.96, 32.38) * mm});
            skArc(sketch, "E91", {"start": v(4.96, 29.15) * mm, "mid": v(5.43, 29.98) * mm, "end": v(4.96, 30.8) * mm});
            skArc(sketch, "E92", {"start": v(4.96, 27.6) * mm, "mid": v(5.32, 28.38) * mm, "end": v(4.96, 29.15) * mm});
            skArc(sketch, "E93", {"start": v(4.96, 26.41) * mm, "mid": v(5.38, 27) * mm, "end": v(4.96, 27.6) * mm});
            skArc(sketch, "E94", {"start": v(4.96, 25.15) * mm, "mid": v(5.33, 25.78) * mm, "end": v(4.96, 26.41) * mm});
            skArc(sketch, "E95", {"start": v(4.96, 23.77) * mm, "mid": v(5.29, 24.46) * mm, "end": v(4.96, 25.15) * mm});
            skArc(sketch, "E96", {"start": v(4.96, 22.3) * mm, "mid": v(5.37, 23.03) * mm, "end": v(4.96, 23.77) * mm});
            skArc(sketch, "E97", {"start": v(4.96, 20.7) * mm, "mid": v(5.44, 21.5) * mm, "end": v(4.96, 22.3) * mm});
            skArc(sketch, "E98", {"start": v(4.96, 19.07) * mm, "mid": v(5.41, 19.89) * mm, "end": v(4.96, 20.7) * mm});
            skArc(sketch, "E99", {"start": v(4.96, 17.33) * mm, "mid": v(5.46, 18.2) * mm, "end": v(4.96, 19.07) * mm});
            skArc(sketch, "E100", {"start": v(4.96, 15.92) * mm, "mid": v(5.35, 16.63) * mm, "end": v(4.96, 17.33) * mm});
            skArc(sketch, "E101", {"start": v(4.96, 14.46) * mm, "mid": v(5.4, 15.19) * mm, "end": v(4.96, 15.92) * mm});
            skArc(sketch, "E102", {"start": v(4.96, 13.1) * mm, "mid": v(5.4, 13.78) * mm, "end": v(4.96, 14.46) * mm});
            skArc(sketch, "E103", {"start": v(4.96, 12) * mm, "mid": v(5.44, 12.56) * mm, "end": v(4.96, 13.1) * mm});
            skLineSegment(sketch, "E104", {"start": v(4.96, 12) * mm, "end": v(5, 3.84) * mm});
            skArc(sketch, "E105", {"start": v(5, 2.61) * mm, "mid": v(5.53, 3.24) * mm, "end": v(5, 3.87) * mm});
            skArc(sketch, "E106", {"start": v(5, 1.25) * mm, "mid": v(5.48, 1.93) * mm, "end": v(5, 2.61) * mm});
            skArc(sketch, "E107", {"start": v(5, -0.17) * mm, "mid": v(5.35, 0.54) * mm, "end": v(5, 1.25) * mm});
            skArc(sketch, "E108", {"start": v(5, -1.61) * mm, "mid": v(5.4, -0.9) * mm, "end": v(5, -0.17) * mm});
            skArc(sketch, "E109", {"start": v(5, -3.19) * mm, "mid": v(5.45, -2.4) * mm, "end": v(5, -1.61) * mm});
            skArc(sketch, "E110", {"start": v(5, -4.84) * mm, "mid": v(5.47, -4.01) * mm, "end": v(5, -3.19) * mm});
            skArc(sketch, "E111", {"start": v(5, -6.51) * mm, "mid": v(5.45, -5.67) * mm, "end": v(5, -4.84) * mm});
            skArc(sketch, "E112", {"start": v(5, -7.81) * mm, "mid": v(5.53, -7.19) * mm, "end": v(5, -6.56) * mm});
            skArc(sketch, "E113", {"start": v(5, -9.18) * mm, "mid": v(5.48, -8.5) * mm, "end": v(5, -7.81) * mm});
            skArc(sketch, "E114", {"start": v(5, -10.6) * mm, "mid": v(5.35, -9.89) * mm, "end": v(5, -9.18) * mm});
            skArc(sketch, "E115", {"start": v(5, -12.04) * mm, "mid": v(5.4, -11.32) * mm, "end": v(5, -10.6) * mm});
            skArc(sketch, "E116", {"start": v(5, -13.61) * mm, "mid": v(5.45, -12.82) * mm, "end": v(5, -12.04) * mm});
            skArc(sketch, "E117", {"start": v(5, -15.26) * mm, "mid": v(5.47, -14.44) * mm, "end": v(5, -13.61) * mm});
            skArc(sketch, "E118", {"start": v(5, -16.94) * mm, "mid": v(5.45, -16.1) * mm, "end": v(5, -15.26) * mm});
            skArc(sketch, "E119", {"start": v(5, -18.41) * mm, "mid": v(5.41, -17.67) * mm, "end": v(5, -16.94) * mm});
            skArc(sketch, "E120", {"start": v(5, -19.81) * mm, "mid": v(5.4, -19.11) * mm, "end": v(5, -18.41) * mm});
            skArc(sketch, "E121", {"start": v(5, -21.07) * mm, "mid": v(5.35, -20.44) * mm, "end": v(5, -19.81) * mm});
            skArc(sketch, "E122", {"start": v(5, -22.12) * mm, "mid": v(5.34, -21.6) * mm, "end": v(5, -21.07) * mm});
            skLineSegment(sketch, "E123", {"start": v(2.53, -22.04) * mm, "end": v(2.53, -13.98) * mm});
            skSolve(sketch);
        }
        {
            var Q0;
            Q0 = qSketchRegion(id + "F8", true);
            var Q1;
            Q1=sQuery(id+"F8.wireOp",EDGE,"E123");
            revolve(context, id + "F9", {"surfaceOperationType" : NewSurfaceOperationType.NEW, "entities" : qUnion([Q0]), "axis" : qUnion([Q1]), "revolveType" : RevolveType.TWO_DIRECTIONS, "angle" : 0 * degree, "angleBack" : 180 * degree});
        }
        {
            var Q0;
            Q0=sQuery(id+"F0.wireOp",EDGE,"E2");
            extrude(context, id + "F10", {"bodyType" : ToolBodyType.SURFACE, "surfaceEntities" : qUnion([Q0]), "depth" : 25.4 * mm, "offsetDistance" : 25.4 * mm});
        }
        {
            var Q0;
            Q0=makeQuery(id+"F9.opRevolve","SWEPT_BODY",BODY,{"disambiguationData":[OSD([sQuery(id+"F8.wireOp",EDGE,"E84"),sQuery(id+"F8.wireOp",EDGE,"E86")])]});
            var Q1;
            Q1=makeQuery(id+"F9.opRevolve","SWEPT_BODY",BODY,{"disambiguationData":[OSD([sQuery(id+"F8.wireOp",EDGE,"E84"),sQuery(id+"F8.wireOp",EDGE,"E87")])]});
            var Q2;
            Q2=makeQuery(id+"F9.opRevolve","SWEPT_BODY",BODY,{"disambiguationData":[OSD([sQuery(id+"F8.wireOp",EDGE,"E84"),sQuery(id+"F8.wireOp",EDGE,"E88")])]});
            var Q3;
            Q3=makeQuery(id+"F9.opRevolve","SWEPT_BODY",BODY,{"disambiguationData":[OSD([sQuery(id+"F8.wireOp",EDGE,"E84"),sQuery(id+"F8.wireOp",EDGE,"E89")])]});
            var Q4;
            Q4=makeQuery(id+"F9.opRevolve","SWEPT_BODY",BODY,{"disambiguationData":[OSD([sQuery(id+"F8.wireOp",EDGE,"E84"),sQuery(id+"F8.wireOp",EDGE,"E91")])]});
            var Q5;
            Q5=makeQuery(id+"F9.opRevolve","SWEPT_BODY",BODY,{"disambiguationData":[OSD([sQuery(id+"F8.wireOp",EDGE,"E84"),sQuery(id+"F8.wireOp",EDGE,"E90")])]});
            var Q6;
            Q6=makeQuery(id+"F9.opRevolve","SWEPT_BODY",BODY,{"disambiguationData":[OSD([sQuery(id+"F8.wireOp",EDGE,"E84"),sQuery(id+"F8.wireOp",EDGE,"E92")])]});
            var Q7;
            Q7=makeQuery(id+"F9.opRevolve","SWEPT_BODY",BODY,{"disambiguationData":[OSD([sQuery(id+"F8.wireOp",EDGE,"E84"),sQuery(id+"F8.wireOp",EDGE,"E93")])]});
            var Q8;
            Q8=makeQuery(id+"F9.opRevolve","SWEPT_BODY",BODY,{"disambiguationData":[OSD([sQuery(id+"F8.wireOp",EDGE,"E84"),sQuery(id+"F8.wireOp",EDGE,"E94")])]});
            var Q9;
            Q9=makeQuery(id+"F9.opRevolve","SWEPT_BODY",BODY,{"disambiguationData":[OSD([sQuery(id+"F8.wireOp",EDGE,"E84"),sQuery(id+"F8.wireOp",EDGE,"E98")])]});
            var Q10;
            Q10=makeQuery(id+"F9.opRevolve","SWEPT_BODY",BODY,{"disambiguationData":[OSD([sQuery(id+"F8.wireOp",EDGE,"E84"),sQuery(id+"F8.wireOp",EDGE,"E97")])]});
            var Q11;
            Q11=makeQuery(id+"F9.opRevolve","SWEPT_BODY",BODY,{"disambiguationData":[OSD([sQuery(id+"F8.wireOp",EDGE,"E84"),sQuery(id+"F8.wireOp",EDGE,"E96")])]});
            var Q12;
            Q12=makeQuery(id+"F9.opRevolve","SWEPT_BODY",BODY,{"disambiguationData":[OSD([sQuery(id+"F8.wireOp",EDGE,"E84"),sQuery(id+"F8.wireOp",EDGE,"E95")])]});
            var Q13;
            Q13=makeQuery(id+"F9.opRevolve","SWEPT_BODY",BODY,{"disambiguationData":[OSD([sQuery(id+"F8.wireOp",EDGE,"E84"),sQuery(id+"F8.wireOp",EDGE,"E99")])]});
            var Q14;
            Q14=makeQuery(id+"F9.opRevolve","SWEPT_BODY",BODY,{"disambiguationData":[OSD([sQuery(id+"F8.wireOp",EDGE,"E84"),sQuery(id+"F8.wireOp",EDGE,"E100")])]});
            var Q15;
            Q15=makeQuery(id+"F9.opRevolve","SWEPT_BODY",BODY,{"disambiguationData":[OSD([sQuery(id+"F8.wireOp",EDGE,"E84"),sQuery(id+"F8.wireOp",EDGE,"E101")])]});
            var Q16;
            Q16=makeQuery(id+"F9.opRevolve","SWEPT_BODY",BODY,{"disambiguationData":[OSD([sQuery(id+"F8.wireOp",EDGE,"E84"),sQuery(id+"F8.wireOp",EDGE,"E102")])]});
            var Q17;
            Q17=makeQuery(id+"F9.opRevolve","SWEPT_BODY",BODY,{"disambiguationData":[OSD([sQuery(id+"F8.wireOp",EDGE,"E84"),sQuery(id+"F8.wireOp",EDGE,"E103")])]});
            var Q18;
            Q18=makeQuery(id+"F9.opRevolve","SWEPT_BODY",BODY,{"disambiguationData":[OSD([sQuery(id+"F8.wireOp",EDGE,"E85"),sQuery(id+"F8.wireOp",EDGE,"E104"),sQuery(id+"F8.wireOp",EDGE,"E105")])]});
            var Q19;
            Q19=makeQuery(id+"F9.opRevolve","SWEPT_BODY",BODY,{"disambiguationData":[OSD([sQuery(id+"F8.wireOp",EDGE,"E85"),sQuery(id+"F8.wireOp",EDGE,"E106")])]});
            var Q20;
            Q20=makeQuery(id+"F9.opRevolve","SWEPT_BODY",BODY,{"disambiguationData":[OSD([sQuery(id+"F8.wireOp",EDGE,"E85"),sQuery(id+"F8.wireOp",EDGE,"E107")])]});
            var Q21;
            Q21=makeQuery(id+"F9.opRevolve","SWEPT_BODY",BODY,{"disambiguationData":[OSD([sQuery(id+"F8.wireOp",EDGE,"E85"),sQuery(id+"F8.wireOp",EDGE,"E108")])]});
            var Q22;
            Q22=makeQuery(id+"F9.opRevolve","SWEPT_BODY",BODY,{"disambiguationData":[OSD([sQuery(id+"F8.wireOp",EDGE,"E85"),sQuery(id+"F8.wireOp",EDGE,"E109")])]});
            var Q23;
            Q23=makeQuery(id+"F9.opRevolve","SWEPT_BODY",BODY,{"disambiguationData":[OSD([sQuery(id+"F8.wireOp",EDGE,"E85"),sQuery(id+"F8.wireOp",EDGE,"E110")])]});
            var Q24;
            Q24=makeQuery(id+"F9.opRevolve","SWEPT_BODY",BODY,{"disambiguationData":[OSD([sQuery(id+"F8.wireOp",EDGE,"E85"),sQuery(id+"F8.wireOp",EDGE,"E112")])]});
            var Q25;
            Q25=makeQuery(id+"F9.opRevolve","SWEPT_BODY",BODY,{"disambiguationData":[OSD([sQuery(id+"F8.wireOp",EDGE,"E85"),sQuery(id+"F8.wireOp",EDGE,"E111")])]});
            var Q26;
            Q26=makeQuery(id+"F9.opRevolve","SWEPT_BODY",BODY,{"disambiguationData":[OSD([sQuery(id+"F8.wireOp",EDGE,"E85"),sQuery(id+"F8.wireOp",EDGE,"E113")])]});
            var Q27;
            Q27=makeQuery(id+"F9.opRevolve","SWEPT_BODY",BODY,{"disambiguationData":[OSD([sQuery(id+"F8.wireOp",EDGE,"E85"),sQuery(id+"F8.wireOp",EDGE,"E116")])]});
            var Q28;
            Q28=makeQuery(id+"F9.opRevolve","SWEPT_BODY",BODY,{"disambiguationData":[OSD([sQuery(id+"F8.wireOp",EDGE,"E85"),sQuery(id+"F8.wireOp",EDGE,"E115")])]});
            var Q29;
            Q29=makeQuery(id+"F9.opRevolve","SWEPT_BODY",BODY,{"disambiguationData":[OSD([sQuery(id+"F8.wireOp",EDGE,"E85"),sQuery(id+"F8.wireOp",EDGE,"E114")])]});
            var Q30;
            Q30=makeQuery(id+"F9.opRevolve","SWEPT_BODY",BODY,{"disambiguationData":[OSD([sQuery(id+"F8.wireOp",EDGE,"E85"),sQuery(id+"F8.wireOp",EDGE,"E118")])]});
            var Q31;
            Q31=makeQuery(id+"F9.opRevolve","SWEPT_BODY",BODY,{"disambiguationData":[OSD([sQuery(id+"F8.wireOp",EDGE,"E85"),sQuery(id+"F8.wireOp",EDGE,"E117")])]});
            var Q32;
            Q32=makeQuery(id+"F9.opRevolve","SWEPT_BODY",BODY,{"disambiguationData":[OSD([sQuery(id+"F8.wireOp",EDGE,"E85"),sQuery(id+"F8.wireOp",EDGE,"E119")])]});
            var Q33;
            Q33=makeQuery(id+"F9.opRevolve","SWEPT_BODY",BODY,{"disambiguationData":[OSD([sQuery(id+"F8.wireOp",EDGE,"E85"),sQuery(id+"F8.wireOp",EDGE,"E120")])]});
            var Q34;
            Q34=makeQuery(id+"F9.opRevolve","SWEPT_BODY",BODY,{"disambiguationData":[OSD([sQuery(id+"F8.wireOp",EDGE,"E85"),sQuery(id+"F8.wireOp",EDGE,"E121")])]});
            var Q35;
            Q35=makeQuery(id+"F9.opRevolve","SWEPT_BODY",BODY,{"disambiguationData":[OSD([sQuery(id+"F8.wireOp",EDGE,"E85"),sQuery(id+"F8.wireOp",EDGE,"E122")])]});
            var Q36;
            Q36=makeQuery(id+"F10.opExtrude","SWEPT_FACE",FACE,{"disambiguationData":[OSD([sQuery(id+"F0.wireOp",EDGE,"E2")])]});
            mirror(context, id + "F11", {"entities" : qUnion([Q0, Q1, Q2, Q3, Q4, Q5, Q6, Q7, Q8, Q9, Q10, Q11, Q12, Q13, Q14, Q15, Q16, Q17, Q18, Q19, Q20, Q21, Q22, Q23, Q24, Q25, Q26, Q27, Q28, Q29, Q30, Q31, Q32, Q33, Q34, Q35]), "mirrorPlane" : qUnion([Q36])});
        }
    });
